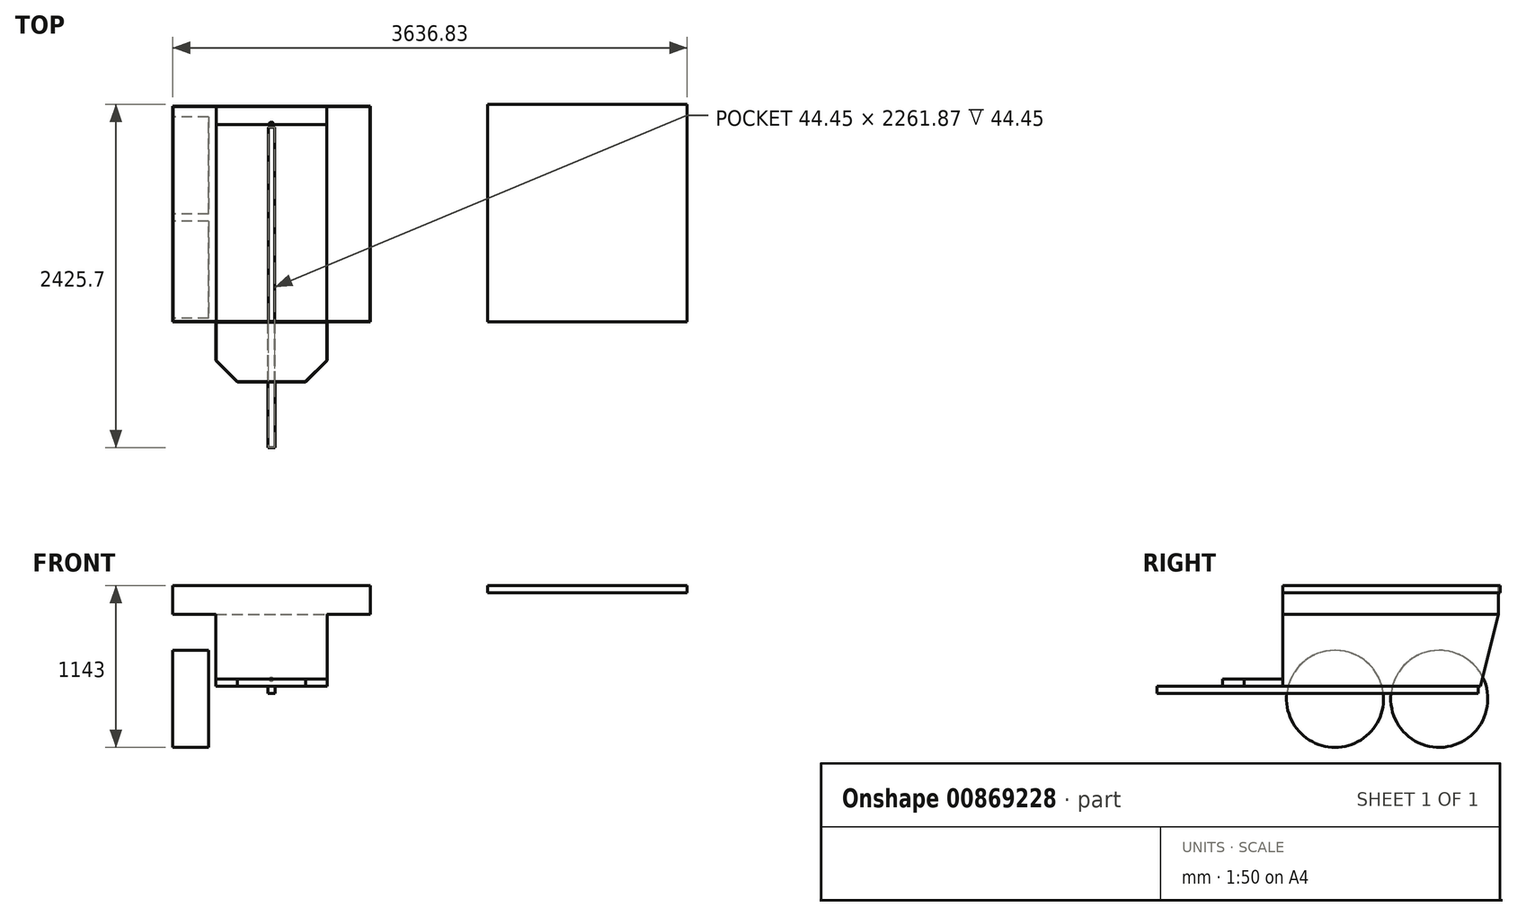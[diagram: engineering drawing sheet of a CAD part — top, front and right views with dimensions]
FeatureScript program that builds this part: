
annotation { "Feature Type Name" : "Feature", "Feature Type Description" : "" }
export const myFeature = defineFeature(function(context is Context, id is Id, definition is map)
    precondition{}
    {
        {
            var Q0;
            Q0=qCreatedBy(makeId("Front.planeOp"),FACE);
            var sketch = newSketch(context, id + "F0", { "sketchPlane" : qUnion([Q0])});
            skLineSegment(sketch, "E0", {"start": v(0, 0) * mm, "end": v(1397, 0) * mm});
            skLineSegment(sketch, "E1", {"start": v(1397, 0) * mm, "end": v(1397, -203.2) * mm});
            skLineSegment(sketch, "E2", {"start": v(0, 0) * mm, "end": v(0, -203.2) * mm});
            skLineSegment(sketch, "E3", {"start": v(0, -203.2) * mm, "end": v(304.8, -203.2) * mm});
            skLineSegment(sketch, "E4", {"start": v(1397, -203.2) * mm, "end": v(1092.2, -203.2) * mm});
            skLineSegment(sketch, "E5", {"start": v(698.5, 0) * mm, "end": v(698.5, -711.2) * mm, "construction": true});
            skLineSegment(sketch, "E6", {"start": v(698.5, -711.2) * mm, "end": v(698.5, -1041.4) * mm, "construction": true});
            skLineSegment(sketch, "E7", {"start": v(1092.2, -203.2) * mm, "end": v(1092.2, -711.2) * mm});
            skLineSegment(sketch, "E8", {"start": v(1092.2, -711.2) * mm, "end": v(304.8, -711.2) * mm});
            skLineSegment(sketch, "E9", {"start": v(304.8, -711.2) * mm, "end": v(304.8, -203.2) * mm});
            skSolve(sketch);
        }
        {
            var Q0;
            Q0 = qSketchRegion(id + "F0", true);
            extrude(context, id + "F1", {"entities" : qUnion([Q0]), "oppositeDirection" : true, "depth" : 1524 * mm, "offsetDistance" : 25.4 * mm});
        }
        {
            var Q0;
            Q0=makeQuery(id+"F1.opExtrude","SWEPT_FACE",FACE,{"disambiguationData":[OSD([sQuery(id+"F0.wireOp",EDGE,"E7")])]});
            var sketch = newSketch(context, id + "F2", { "sketchPlane" : qUnion([Q0])});
            skLineSegment(sketch, "E10", {"start": v(0, -203.2) * mm, "end": v(508, -711.2) * mm});
            skLineSegment(sketch, "E11", {"start": v(1524, -203.2) * mm, "end": v(1397, -711.2) * mm});
            skSolve(sketch);
        }
        {
            var Q0;
            {var subQ0=sQuery(id+"F2.wireOp",EDGE,"E11");Q0=makeQuery(id+"F2.imprint","IMPRINT",FACE,{"disambiguationData":[TD([[makeQuery(id+"F2.imprint","IMPRINT",EDGE,{"derivedFrom":subQ0}),1.0]])]});}
            extrude(context, id + "F3", {"entities" : qUnion([Q0]), "operationType" : NewBodyOperationType.REMOVE, "endBound" : BoundingType.THROUGH_ALL, "oppositeDirection" : true, "depth" : 25.4 * mm, "offsetDistance" : 25.4 * mm});
        }
        {
            var Q0;
            Q0=makeQuery(id+"F1.opExtrude","CAP_FACE",FACE,{"disambiguationData":[OSD([sQuery(id+"F0.wireOp",EDGE,"E0"),sQuery(id+"F0.wireOp",EDGE,"E1"),sQuery(id+"F0.wireOp",EDGE,"E2"),sQuery(id+"F0.wireOp",EDGE,"E3"),sQuery(id+"F0.wireOp",EDGE,"E4"),sQuery(id+"F0.wireOp",EDGE,"E7"),sQuery(id+"F0.wireOp",EDGE,"E8"),sQuery(id+"F0.wireOp",EDGE,"E9")])],"isStart":true});
            var sketch = newSketch(context, id + "F4", { "sketchPlane" : qUnion([Q0])});
            skLineSegment(sketch, "E12", {"start": v(698.5, -711.2) * mm, "end": v(723.9, -711.2) * mm});
            skLineSegment(sketch, "E13", {"start": v(723.9, -711.2) * mm, "end": v(723.9, -762) * mm});
            skLineSegment(sketch, "E14", {"start": v(723.9, -762) * mm, "end": v(673.1, -762) * mm});
            skLineSegment(sketch, "E15", {"start": v(673.1, -762) * mm, "end": v(673.1, -711.2) * mm});
            skLineSegment(sketch, "E16", {"start": v(673.1, -711.2) * mm, "end": v(698.5, -711.2) * mm});
            skSolve(sketch);
        }
        {
            var Q0;
            Q0 = qSketchRegion(id + "F4", true);
            extrude(context, id + "F5", {"entities" : qUnion([Q0]), "operationType" : NewBodyOperationType.ADD, "depth" : 889 * mm, "offsetDistance" : 25.4 * mm, "hasSecondDirection" : true, "secondDirectionOppositeDirection" : true, "secondDirectionDepth" : 1379.22 * mm});
        }
        {
            var Q0;
            Q0=makeQuery(id+"F1.opExtrude","SWEPT_FACE",FACE,{"disambiguationData":[OSD([sQuery(id+"F0.wireOp",EDGE,"E2")])]});
            var sketch = newSketch(context, id + "F6", { "sketchPlane" : qUnion([Q0])});
            skCircle(sketch, "E17", {"center": v(-1104.9, -800.1) * mm, "radius": 342.9 * mm});
            skCircle(sketch, "E18", {"center": v(-368.3, -800.1) * mm, "radius": 342.9 * mm});
            skSolve(sketch);
        }
        {
            var Q0;
            Q0 = qSketchRegion(id + "F6", true);
            extrude(context, id + "F7", {"entities" : qUnion([Q0]), "oppositeDirection" : true, "depth" : 254 * mm, "offsetDistance" : 25.4 * mm});
        }
        {
            var Q0;
            Q0=makeQuery(id+"F1.opExtrude","SWEPT_FACE",FACE,{"disambiguationData":[OSD([sQuery(id+"F0.wireOp",EDGE,"E8")])]});
            var sketch = newSketch(context, id + "F8", { "sketchPlane" : qUnion([Q0])});
            skLineSegment(sketch, "E19.bottom", {"start": v(304.8, 0) * mm, "end": v(1092.2, 0) * mm});
            skLineSegment(sketch, "E19.top", {"start": v(457.2, 425.72) * mm, "end": v(939.8, 425.72) * mm});
            skLineSegment(sketch, "E19.left", {"start": v(304.8, 0) * mm, "end": v(304.8, 273.32) * mm});
            skLineSegment(sketch, "E19.right", {"start": v(1092.2, 0) * mm, "end": v(1092.2, 273.32) * mm});
            skLineSegment(sketch, "E20", {"start": v(939.8, 425.72) * mm, "end": v(1092.2, 273.32) * mm});
            skLineSegment(sketch, "E21", {"start": v(457.2, 425.72) * mm, "end": v(304.8, 273.32) * mm});
            skPoint(sketch, "E22.orphan", {"position": v(304.8, 425.72) * mm});
            skPoint(sketch, "E23.orphan", {"position": v(1092.2, 425.72) * mm});
            skSolve(sketch);
        }
        {
            var Q0;
            Q0=makeQuery(id+"F8.imprint","IMPRINT",FACE,{"disambiguationData":[TD([[makeQuery(id+"F8.imprint","IMPRINT",EDGE,{"derivedFrom":sQuery(id+"F8.wireOp",EDGE,"E19.top")}),-1.0]])]});
            extrude(context, id + "F9", {"entities" : qUnion([Q0]), "oppositeDirection" : true, "depth" : 50.8 * mm, "offsetDistance" : 25.4 * mm});
        }
        {
            var Q0;
            Q0=makeQuery(id+"F9.opExtrude","CAP_FACE",FACE,{"disambiguationData":[OSD([sQuery(id+"F8.wireOp",EDGE,"E19.bottom"),sQuery(id+"F8.wireOp",EDGE,"E19.top"),sQuery(id+"F8.wireOp",EDGE,"E19.left"),sQuery(id+"F8.wireOp",EDGE,"E19.right"),sQuery(id+"F8.wireOp",EDGE,"E20"),sQuery(id+"F8.wireOp",EDGE,"E21")])],"isStart":false});
            shell(context, id + "F10", {"entities" : qUnion([Q0]), "thickness" : 3.17 * mm});
        }
        {
            var Q0;
            Q0=makeQuery(id+"F1.opExtrude","SWEPT_FACE",FACE,{"disambiguationData":[OSD([sQuery(id+"F0.wireOp",EDGE,"E0")])]});
            shell(context, id + "F11", {"entities" : qUnion([Q0]), "thickness" : 3.17 * mm});
        }
        {
            var Q0;
            Q0=makeQuery(id+"F3.boolean.opBoolean","COPY",FACE,{"derivedFrom":makeQuery(id+"F3.opExtrude","SWEPT_FACE",FACE,{"disambiguationData":[OSD([sQuery(id+"F2.wireOp",EDGE,"E11")])]})});
            var sketch = newSketch(context, id + "F12", { "sketchPlane" : qUnion([Q0])});
            skCircle(sketch, "E24", {"center": v(-698.5, -300.78) * mm, "radius": 12.7 * mm});
            skPoint(sketch, "E24.centerSnap0", {"position": v(-698.5, -351.14) * mm});
            skSolve(sketch);
        }
        {
            var Q0;
            Q0 = qSketchRegion(id + "F12", true);
            extrude(context, id + "F13", {"entities" : qUnion([Q0]), "operationType" : NewBodyOperationType.REMOVE, "oppositeDirection" : true, "depth" : 25.4 * mm, "offsetDistance" : 25.4 * mm});
        }
        {
            var Q0;
            Q0=makeQuery(id+"F1.opExtrude","CAP_FACE",FACE,{"disambiguationData":[OSD([sQuery(id+"F0.wireOp",EDGE,"E0"),sQuery(id+"F0.wireOp",EDGE,"E1"),sQuery(id+"F0.wireOp",EDGE,"E2"),sQuery(id+"F0.wireOp",EDGE,"E3"),sQuery(id+"F0.wireOp",EDGE,"E4"),sQuery(id+"F0.wireOp",EDGE,"E7"),sQuery(id+"F0.wireOp",EDGE,"E8"),sQuery(id+"F0.wireOp",EDGE,"E9")])],"isStart":true});
            var sketch = newSketch(context, id + "F14", { "sketchPlane" : qUnion([Q0])});
            skLineSegment(sketch, "E25", {"start": v(2227.13, 0) * mm, "end": v(3636.83, 0) * mm});
            skLineSegment(sketch, "E26", {"start": v(2227.13, 0) * mm, "end": v(2227.13, -50.8) * mm});
            skLineSegment(sketch, "E27", {"start": v(2227.13, -50.8) * mm, "end": v(3636.83, -50.8) * mm});
            skLineSegment(sketch, "E28", {"start": v(3636.83, -50.8) * mm, "end": v(3636.83, 0) * mm});
            skSolve(sketch);
        }
        {
            var Q0;
            Q0 = qSketchRegion(id + "F14", true);
            extrude(context, id + "F15", {"entities" : qUnion([Q0]), "oppositeDirection" : true, "depth" : 1536.7 * mm, "offsetDistance" : 25.4 * mm});
        }
        {
            var Q0;
            Q0=makeQuery(id+"F15.opExtrude","SWEPT_FACE",FACE,{"disambiguationData":[OSD([sQuery(id+"F14.wireOp",EDGE,"E27")])]});
            shell(context, id + "F16", {"entities" : qUnion([Q0]), "thickness" : 3.17 * mm});
        }
    });
